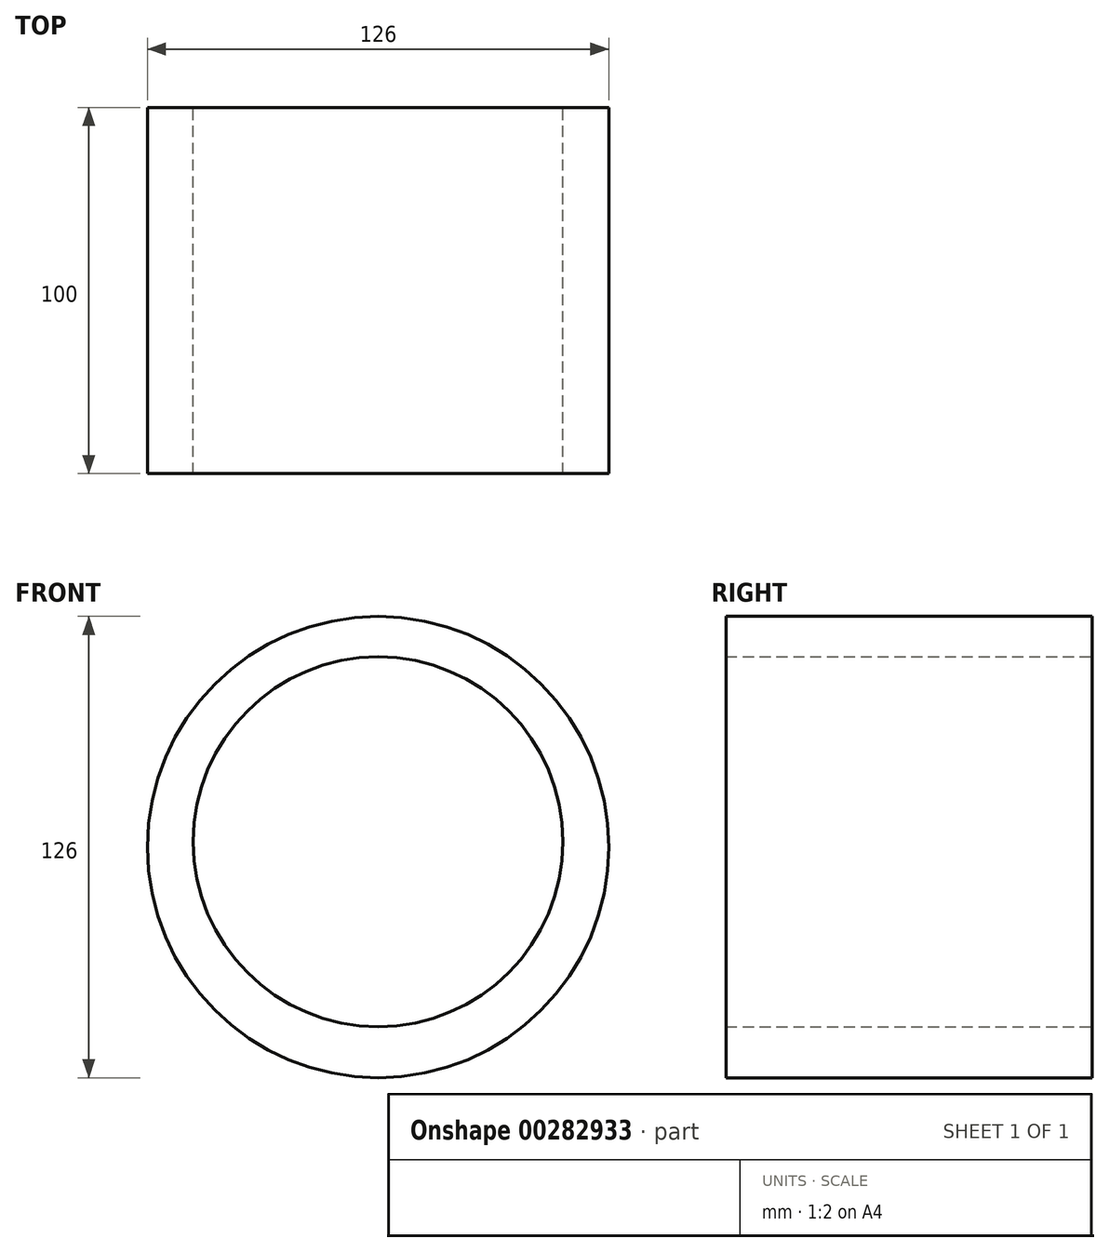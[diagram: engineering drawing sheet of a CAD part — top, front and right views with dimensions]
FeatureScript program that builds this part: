
annotation { "Feature Type Name" : "Feature", "Feature Type Description" : "" }
export const myFeature = defineFeature(function(context is Context, id is Id, definition is map)
    precondition{}
    {
        {
            var Q0;
            Q0=qCreatedBy(makeId("Front.planeOp"),FACE);
            var sketch = newSketch(context, id + "F0", { "sketchPlane" : qUnion([Q0])});
            skCircle(sketch, "E0", {"center": v(0, 0) * mm, "radius": 50.5 * mm});
            skCircle(sketch, "E1", {"center": v(0, -1.47) * mm, "radius": 63 * mm});
            skSolve(sketch);
        }
        {
            var Q0;
            Q0=makeQuery(id+"F0.imprint","IMPRINT",FACE,{"disambiguationData":[TD([[makeQuery(id+"F0.imprint","IMPRINT",EDGE,{"derivedFrom":sQuery(id+"F0.wireOp",EDGE,"E0")}),-1.0]])]});
            extrude(context, id + "F1", {"entities" : qUnion([Q0]), "depth" : 100 * mm});
        }
    });
